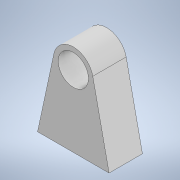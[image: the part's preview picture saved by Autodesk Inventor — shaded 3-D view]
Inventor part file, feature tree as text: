
AUTODESK INVENTOR PART (.ipt)
format: ipt  version: 2021 (Build 250183000, 183)  size: 101,888 bytes
history: native  units: in
note: dims shown in document units (in); Inventor stores cm internally (conversion verified against a paired STEP export)
features: other x1, extrude x1, sketch x1
ambient origin geometry x8: Origin, YZ Plane, XZ Plane, XY Plane, X Axis, Y Axis, Z Axis, Center Point
bodies: Body1 (feature_tree)
feature tree (3):
  other  "Sólido1"
  extrude  "Extrusión1"  Depth=0.2756in
  sketch  "Boceto1"  dims[d0=0.25in d1=0.0394in d2=0.5906in d3=0.2953in d4=0.2953in d5=0.2756in d6=0.0in]
